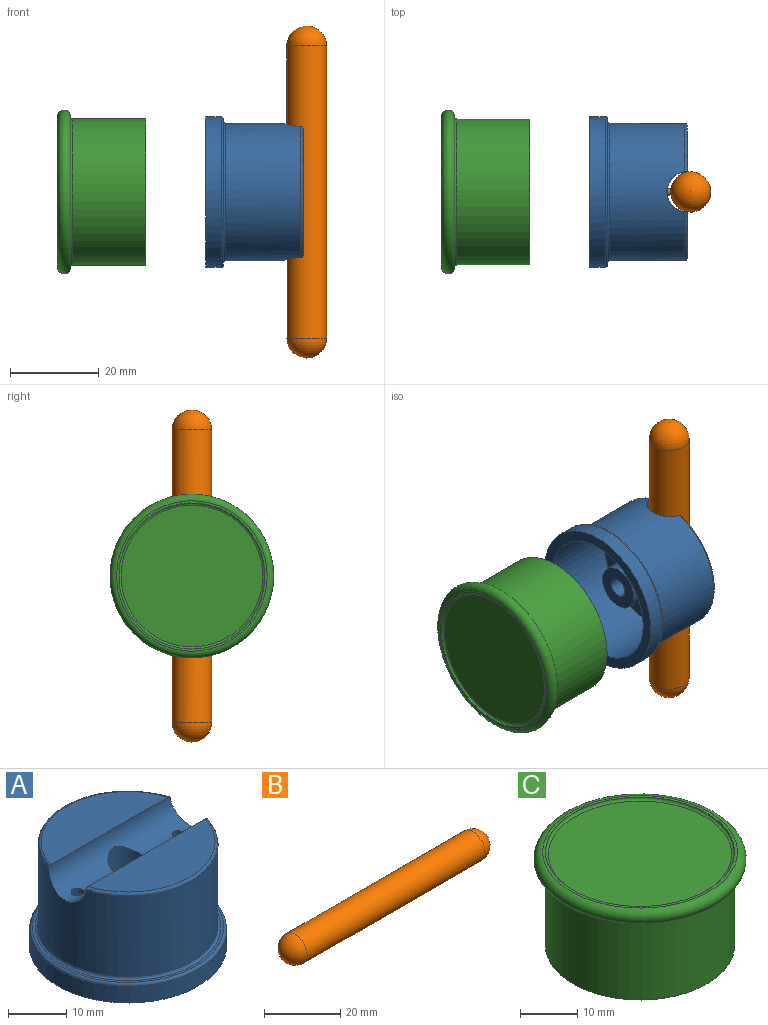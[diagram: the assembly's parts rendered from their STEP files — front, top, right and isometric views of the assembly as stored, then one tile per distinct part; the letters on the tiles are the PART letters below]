
ASSEMBLY  parts=3 mates=3
PART A: 20 faces, bbox 36.8x36.8x22 mm
  f0: cylinder r=4.55mm len=31mm, axis (-1,0,0), area 383.6mm2, adj f1,f2,f3,f4,f5,f11,f12,f17
  f1: cylinder r=1mm len=2mm, axis (0,0,-1), area 6.3mm2, adj f0,f14
  f2: cylinder r=1.14mm len=2.29mm, axis (0,0,-1), area 7.4mm2, adj f0,f14
  f3: plane 28.59x10.45mm, normal (0,0,1), area 219.1mm2, adj f0,f12
  f4: torus R=15mm, axis (0,0,1), area 30.5mm2, adj f0,f5,f11
  f5: plane 28.59x10.45mm, normal (0,0,1), area 219.1mm2, adj f0,f4
  f6: plane 34x34mm, normal (0,0,-1), area 247.4mm2, adj f7,f13
  f7: cylinder r=17mm len=34mm, axis (0,0,1), area 373.8mm2, adj f6,f8
  f8: torus R=16.5mm, axis (0,0,1), area 83mm2, adj f7,f9
  f9: plane 33x33mm, normal (0,0,1), area 51.1mm2, adj f8,f10
  f10: torus R=16mm, axis (0,0,1), area 77.4mm2, adj f9,f11
  f11: cylinder r=15.5mm len=31mm, axis (0,0,1), area 1599.1mm2, adj f0,f4,f10,f12
  f12: torus R=15mm, axis (0,0,1), area 30.5mm2, adj f0,f3,f11
  f13: cylinder r=14.5mm len=29mm, axis (0,0,-1), area 1503.3mm2, adj f6,f14
  f14: plane 29x29mm, normal (0,0,-1), area 574.7mm2, adj f1,f2,f13,f15
  f15: cylinder r=5mm len=10mm, axis (0,0,1), area 314.2mm2, adj f14,f16
  f16: plane 10x10mm, normal (0,0,-1), area 64.7mm2, adj f15,f18
  f17: cylinder r=3.5mm len=9.59mm, axis (0,0,1), area 191.9mm2, adj f0,f19
  f18: cylinder r=2.1mm len=4.2mm, axis (0,0,1), area 39.6mm2, adj f16,f19
  f19: plane 7x7mm, normal (0,0,1), area 24.6mm2, adj f17,f18
PART B: 7 faces, bbox 75x9x10.5 mm
  f0: cylinder r=4.5mm len=66mm, axis (-1,0,0), area 1862.6mm2, adj f1,f2,f3,f5
  f1: sphere r=4.5mm, area 127.2mm2, adj f0
  f2: sphere r=4.5mm, area 127.2mm2, adj f0
  f3: cylinder r=0.75mm len=1.5mm, axis (0,0,1), area 3.7mm2, adj f0,f4
  f4: sphere r=0.75mm, area 3.5mm2, adj f3
  f5: cylinder r=0.75mm len=1.5mm, axis (0,0,1), area 3.7mm2, adj f0,f6
  f6: sphere r=0.75mm, area 3.5mm2, adj f5
PART C: 13 faces, bbox 40x40x20.4 mm
  f0: torus R=17mm, axis (0,0,1), area 82.3mm2, adj f1,f6
  f1: torus R=17mm, axis (0,0,1), area 531.6mm2, adj f0,f2
  f2: plane 34x34mm, normal (0,0,1), area 52.6mm2, adj f1,f3
  f3: torus R=16mm, axis (0,0,1), area 80.5mm2, adj f2,f4
  f4: plane 32x32mm, normal (0,0,1), area 804.2mm2, adj f3
  f5: plane 33x33mm, normal (0,0,-1), area 194.8mm2, adj f6,f7
  f6: cylinder r=16.5mm len=33mm, axis (0,0,1), area 1710.6mm2, adj f0,f5
  f7: cylinder r=14.5mm len=29mm, axis (0,0,-1), area 1366.6mm2, adj f5,f8
  f8: plane 29x29mm, normal (0,0,-1), area 582mm2, adj f7,f9
  f9: cylinder r=5mm len=10mm, axis (0,0,1), area 314.2mm2, adj f8,f10
  f10: plane 10x10mm, normal (0,0,-1), area 64.7mm2, adj f9,f12
  f11: cone r=0mm half-angle=59deg, axis (0,0,-1), area 16.2mm2, adj f12
  f12: cylinder r=2.1mm len=11mm, axis (0,0,-1), area 145.1mm2, adj f10,f11
PLACE A rot(axis=(0,1,0),90deg) t=(-15.22,-1.1,9.55)mm
PLACE B rot(axis=(-0.71,0,-0.71),180deg) t=(7.6,-1.1,9.55)mm
PLACE C rot(axis=(0.58,-0.58,-0.58),120deg) t=(-28.72,-1.1,9.55)mm
MATE fastened C.f0 <-> A.f15  axis (1,0,0) through (-33.72,-1.1,9.55)mm
MATE fastened A.f1 <-> B.f5  axis (-1,0,0) through (2.35,-1.1,-2.7)mm
MATE fastened A.f1 <-> B.f5  axis (-1,0,0) through (2.35,-1.1,-2.7)mm
